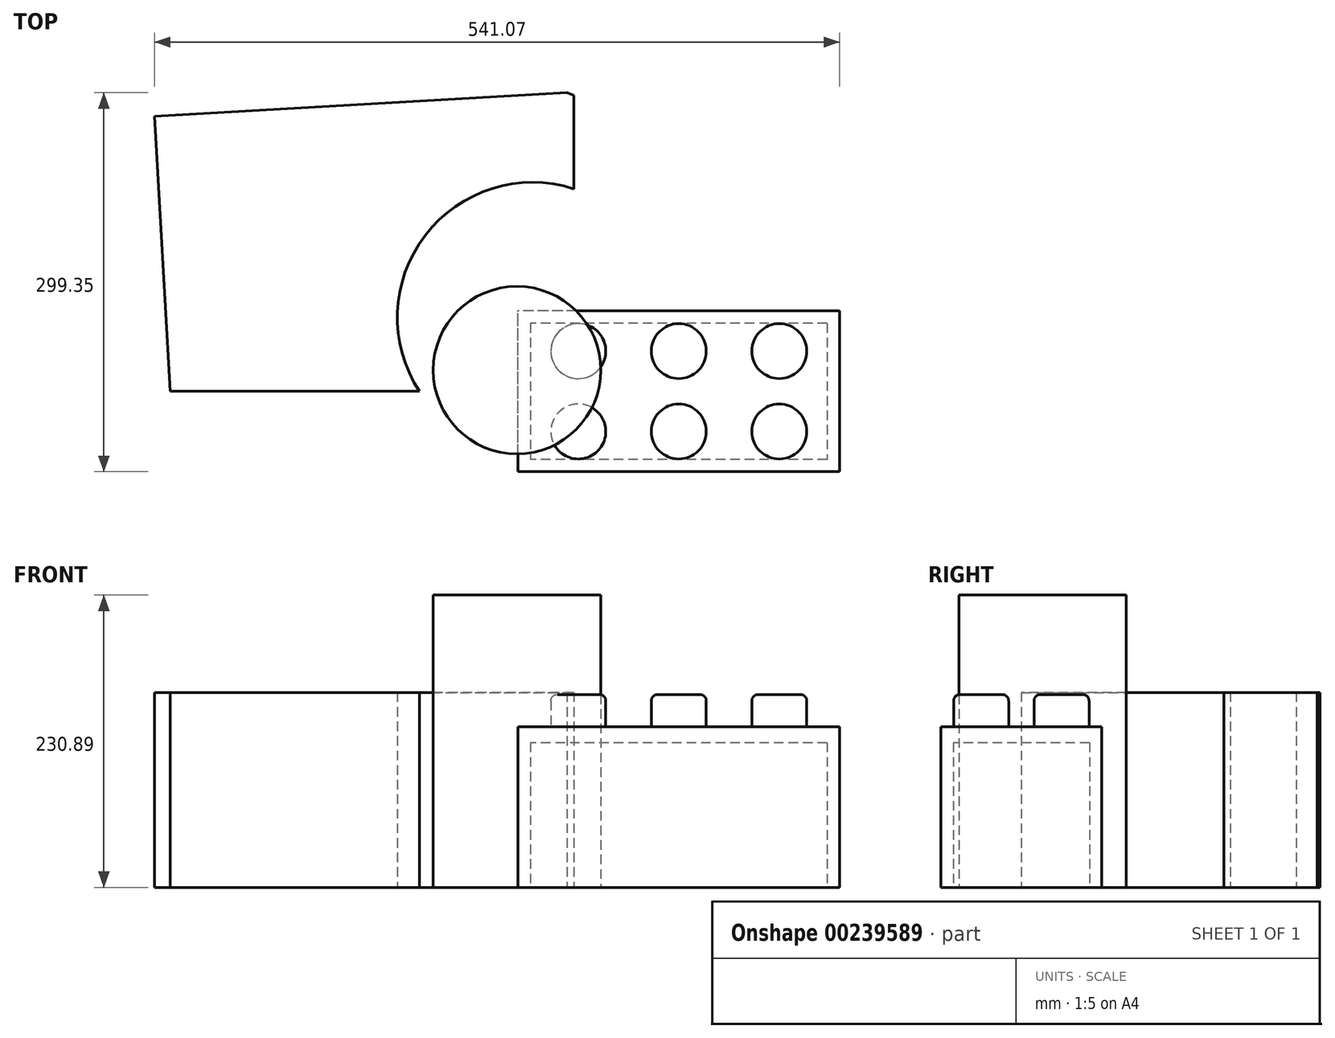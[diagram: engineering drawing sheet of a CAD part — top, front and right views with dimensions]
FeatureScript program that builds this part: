
annotation { "Feature Type Name" : "Feature", "Feature Type Description" : "" }
export const myFeature = defineFeature(function(context is Context, id is Id, definition is map)
    precondition{}
    {
        {
            var Q0;
            Q0=qCreatedBy(makeId("Top.planeOp"),FACE);
            var sketch = newSketch(context, id + "F0", { "sketchPlane" : qUnion([Q0])});
            skLineSegment(sketch, "E0.bottom", {"start": v(127, -63.5) * mm, "end": v(-127, -63.5) * mm});
            skLineSegment(sketch, "E0.top", {"start": v(127, 63.5) * mm, "end": v(-127, 63.5) * mm});
            skLineSegment(sketch, "E0.left", {"start": v(127, -63.5) * mm, "end": v(127, 63.5) * mm});
            skLineSegment(sketch, "E0.right", {"start": v(-127, -63.5) * mm, "end": v(-127, 63.5) * mm});
            skPoint(sketch, "E0.middle", {"position": v(0, 0) * mm});
            skSolve(sketch);
        }
        {
            var Q0;
            Q0=makeQuery(id+"F0.imprint","IMPRINT",FACE,{"disambiguationData":[TD([[makeQuery(id+"F0.imprint","IMPRINT",EDGE,{"derivedFrom":sQuery(id+"F0.wireOp",EDGE,"E0.bottom")}),-1.0]])]});
            extrude(context, id + "F1", {"entities" : qUnion([Q0]), "depth" : 127 * mm});
        }
        {
            var Q0;
            Q0=makeQuery(id+"F1.opExtrude","CAP_FACE",FACE,{"disambiguationData":[OSD([sQuery(id+"F0.wireOp",EDGE,"E0.bottom"),sQuery(id+"F0.wireOp",EDGE,"E0.top"),sQuery(id+"F0.wireOp",EDGE,"E0.left"),sQuery(id+"F0.wireOp",EDGE,"E0.right")])],"isStart":false});
            var sketch = newSketch(context, id + "F2", { "sketchPlane" : qUnion([Q0])});
            skCircle(sketch, "E1", {"center": v(-79.37, -31.75) * mm, "radius": 21.71 * mm});
            skCircle(sketch, "E2", {"center": v(-79.38, 31.75) * mm, "radius": 21.71 * mm});
            skCircle(sketch, "E3", {"center": v(0, 31.75) * mm, "radius": 21.71 * mm});
            skCircle(sketch, "E4", {"center": v(0, -31.75) * mm, "radius": 21.71 * mm});
            skCircle(sketch, "E5", {"center": v(79.38, -31.75) * mm, "radius": 21.71 * mm});
            skCircle(sketch, "E6", {"center": v(79.38, 31.75) * mm, "radius": 21.71 * mm});
            skLineSegment(sketch, "E7", {"start": v(-79.38, 31.75) * mm, "end": v(198.43, 31.75) * mm, "construction": true});
            skLineSegment(sketch, "E8", {"start": v(-79.37, -31.75) * mm, "end": v(195.1, -31.75) * mm, "construction": true});
            skLineSegment(sketch, "E9", {"start": v(-79.38, 92.38) * mm, "end": v(-79.37, -101.2) * mm, "construction": true});
            skLineSegment(sketch, "E10", {"start": v(0, 104.83) * mm, "end": v(0, -110.19) * mm, "construction": true});
            skLineSegment(sketch, "E11", {"start": v(79.37, 111.11) * mm, "end": v(79.38, -99.71) * mm, "construction": true});
            skSolve(sketch);
        }
        {
            var Q0;
            Q0=makeQuery(id+"F2.imprint","IMPRINT",FACE,{"disambiguationData":[TD([[makeQuery(id+"F2.imprint","IMPRINT",EDGE,{"derivedFrom":sQuery(id+"F2.wireOp",EDGE,"E2")}),1.0]])]});
            var Q1;
            Q1=makeQuery(id+"F2.imprint","IMPRINT",FACE,{"disambiguationData":[TD([[makeQuery(id+"F2.imprint","IMPRINT",EDGE,{"derivedFrom":sQuery(id+"F2.wireOp",EDGE,"E3")}),1.0]])]});
            var Q2;
            Q2=makeQuery(id+"F2.imprint","IMPRINT",FACE,{"disambiguationData":[TD([[makeQuery(id+"F2.imprint","IMPRINT",EDGE,{"derivedFrom":sQuery(id+"F2.wireOp",EDGE,"E6")}),1.0]])]});
            var Q3;
            Q3=makeQuery(id+"F2.imprint","IMPRINT",FACE,{"disambiguationData":[TD([[makeQuery(id+"F2.imprint","IMPRINT",EDGE,{"derivedFrom":sQuery(id+"F2.wireOp",EDGE,"E5")}),1.0]])]});
            var Q4;
            Q4=makeQuery(id+"F2.imprint","IMPRINT",FACE,{"disambiguationData":[TD([[makeQuery(id+"F2.imprint","IMPRINT",EDGE,{"derivedFrom":sQuery(id+"F2.wireOp",EDGE,"E4")}),1.0]])]});
            var Q5;
            Q5=makeQuery(id+"F2.imprint","IMPRINT",FACE,{"disambiguationData":[TD([[makeQuery(id+"F2.imprint","IMPRINT",EDGE,{"derivedFrom":sQuery(id+"F2.wireOp",EDGE,"E1")}),1.0]])]});
            extrude(context, id + "F3", {"entities" : qUnion([Q0, Q1, Q2, Q3, Q4, Q5]), "operationType" : NewBodyOperationType.ADD, "depth" : 25.4 * mm});
        }
        {
            var Q0;
            Q0=makeQuery(id+"F1.opExtrude","CAP_FACE",FACE,{"disambiguationData":[OSD([sQuery(id+"F0.wireOp",EDGE,"E0.bottom"),sQuery(id+"F0.wireOp",EDGE,"E0.top"),sQuery(id+"F0.wireOp",EDGE,"E0.left"),sQuery(id+"F0.wireOp",EDGE,"E0.right")])],"isStart":true});
            var sketch = newSketch(context, id + "F4", { "sketchPlane" : qUnion([Q0])});
            skLineSegment(sketch, "E12.bottom", {"start": v(117.16, -53.79) * mm, "end": v(-117.16, -53.79) * mm});
            skLineSegment(sketch, "E12.top", {"start": v(117.16, 53.79) * mm, "end": v(-117.16, 53.79) * mm});
            skLineSegment(sketch, "E12.left", {"start": v(117.16, -53.79) * mm, "end": v(117.16, 53.79) * mm});
            skLineSegment(sketch, "E12.right", {"start": v(-117.16, -53.79) * mm, "end": v(-117.16, 53.79) * mm});
            skPoint(sketch, "E12.middle", {"position": v(0, 0) * mm});
            skSolve(sketch);
        }
        {
            var Q0;
            Q0 = qSketchRegion(id + "F4", true);
            extrude(context, id + "F5", {"entities" : qUnion([Q0]), "operationType" : NewBodyOperationType.REMOVE, "oppositeDirection" : true, "depth" : 114.3 * mm});
        }
        {
            var Q0;
            Q0=makeQuery(id+"F3.opExtrude","CAP_EDGE",EDGE,{"disambiguationData":[OSD([sQuery(id+"F2.wireOp",EDGE,"E6")])],"isStart":false});
            var Q1;
            Q1=makeQuery(id+"F3.opExtrude","CAP_EDGE",EDGE,{"disambiguationData":[OSD([sQuery(id+"F2.wireOp",EDGE,"E3")])],"isStart":false});
            var Q2;
            Q2=makeQuery(id+"F3.opExtrude","CAP_EDGE",EDGE,{"disambiguationData":[OSD([sQuery(id+"F2.wireOp",EDGE,"E2")])],"isStart":false});
            var Q3;
            Q3=makeQuery(id+"F3.opExtrude","CAP_FACE",FACE,{"disambiguationData":[OSD([sQuery(id+"F2.wireOp",EDGE,"E1")])],"isStart":false});
            var Q4;
            Q4=makeQuery(id+"F3.opExtrude","CAP_FACE",FACE,{"disambiguationData":[OSD([sQuery(id+"F2.wireOp",EDGE,"E4")])],"isStart":false});
            var Q5;
            Q5=makeQuery(id+"F3.opExtrude","CAP_FACE",FACE,{"disambiguationData":[OSD([sQuery(id+"F2.wireOp",EDGE,"E5")])],"isStart":false});
            fillet(context, id + "F6", {"entities" : qUnion([Q0, Q1, Q2, Q3, Q4, Q5]), "radius" : 5.08 * mm, "tangentPropagation" : true, "allowEdgeOverflow" : false});
        }
        {
            var Q0;
            Q0=qCreatedBy(makeId("Top.planeOp"),FACE);
            var sketch = newSketch(context, id + "F7", { "sketchPlane" : qUnion([Q0])});
            skLineSegment(sketch, "E13", {"start": v(-204.83, 0) * mm, "end": v(-401.59, 0) * mm});
            skLineSegment(sketch, "E14", {"start": v(-401.59, 0) * mm, "end": v(-414.07, 217.13) * mm});
            skLineSegment(sketch, "E15", {"start": v(-414.07, 217.13) * mm, "end": v(-88.28, 235.85) * mm});
            skLineSegment(sketch, "E16", {"start": v(-88.28, 235.85) * mm, "end": v(-82.77, 233.65) * mm});
            skLineSegment(sketch, "E17", {"start": v(-82.77, 233.65) * mm, "end": v(-82.77, 159.91) * mm});
            skArc(sketch, "E18", {"start": v(-82.77, 159.91) * mm, "mid": v(-200.35, 123.12) * mm, "end": v(-204.83, 0) * mm});
            skSolve(sketch);
        }
        {
            var Q0;
            Q0=makeQuery(id+"F7.imprint","IMPRINT",FACE,{"disambiguationData":[TD([[makeQuery(id+"F7.imprint","IMPRINT",EDGE,{"derivedFrom":sQuery(id+"F7.wireOp",EDGE,"E13")}),-1.0]])]});
            extrude(context, id + "F8", {"entities" : qUnion([Q0]), "depth" : 153.92 * mm});
        }
        {
            var Q0;
            Q0=qCreatedBy(makeId("Top.planeOp"),FACE);
            var sketch = newSketch(context, id + "F9", { "sketchPlane" : qUnion([Q0])});
            skCircle(sketch, "E19", {"center": v(-127.83, 16.74) * mm, "radius": 66.15 * mm});
            skSolve(sketch);
        }
        {
            var Q0;
            Q0 = qSketchRegion(id + "F9", true);
            extrude(context, id + "F10", {"entities" : qUnion([Q0]), "depth" : 230.89 * mm});
        }
    });
